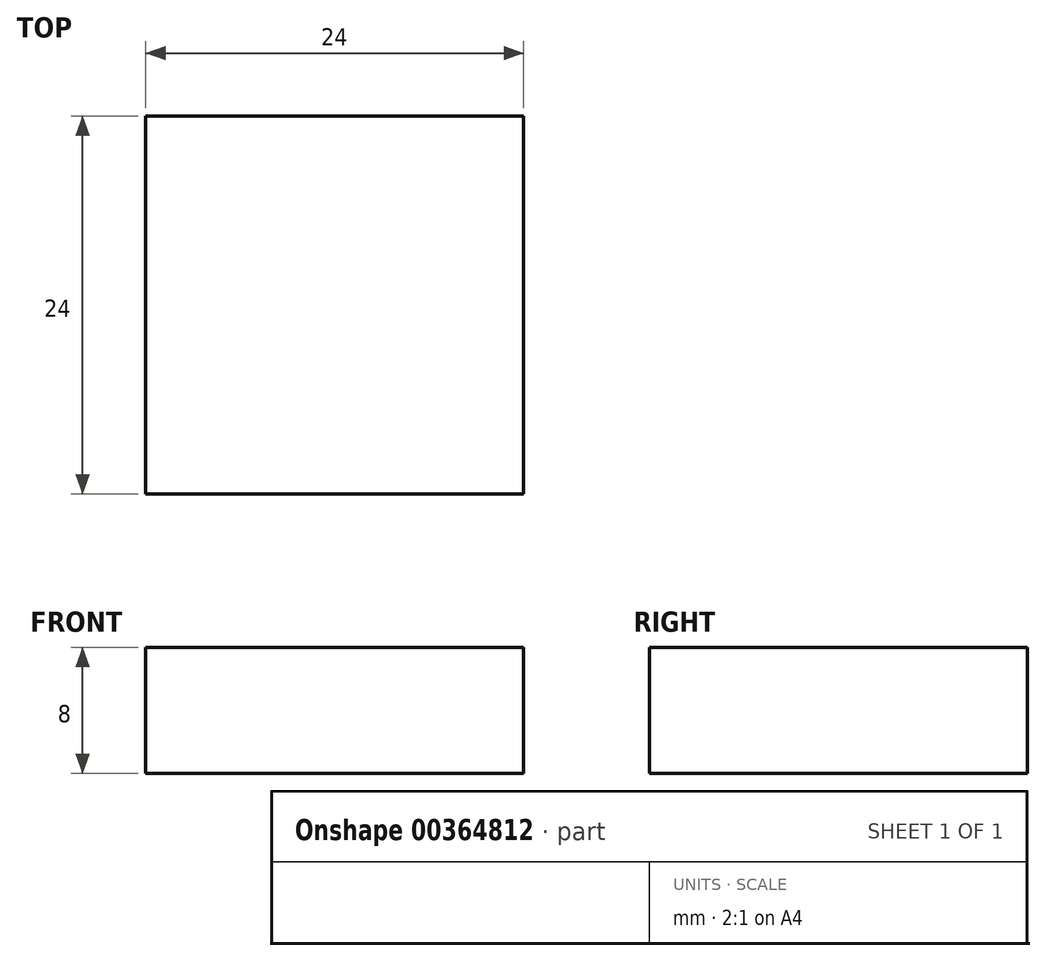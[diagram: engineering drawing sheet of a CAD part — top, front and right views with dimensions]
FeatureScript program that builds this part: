
annotation { "Feature Type Name" : "Feature", "Feature Type Description" : "" }
export const myFeature = defineFeature(function(context is Context, id is Id, definition is map)
    precondition{}
    {
        {
            var Q0;
            Q0=qCreatedBy(makeId("Top.planeOp"),FACE);
            var sketch = newSketch(context, id + "F0", { "sketchPlane" : qUnion([Q0])});
            skLineSegment(sketch, "E0.bottom", {"start": v(12, -12) * mm, "end": v(-12, -12) * mm});
            skLineSegment(sketch, "E0.top", {"start": v(12, 12) * mm, "end": v(-12, 12) * mm});
            skLineSegment(sketch, "E0.left", {"start": v(12, -12) * mm, "end": v(12, 12) * mm});
            skLineSegment(sketch, "E0.right", {"start": v(-12, -12) * mm, "end": v(-12, 12) * mm});
            skPoint(sketch, "E0.middle", {"position": v(0, 0) * mm});
            skSolve(sketch);
        }
        {
            var Q0;
            Q0=makeQuery(id+"F0.imprint","IMPRINT",FACE,{"disambiguationData":[TD([[makeQuery(id+"F0.imprint","IMPRINT",EDGE,{"derivedFrom":sQuery(id+"F0.wireOp",EDGE,"E0.bottom")}),-1.0]])]});
            extrude(context, id + "F1", {"entities" : qUnion([Q0]), "depth" : 8 * mm});
        }
    });
